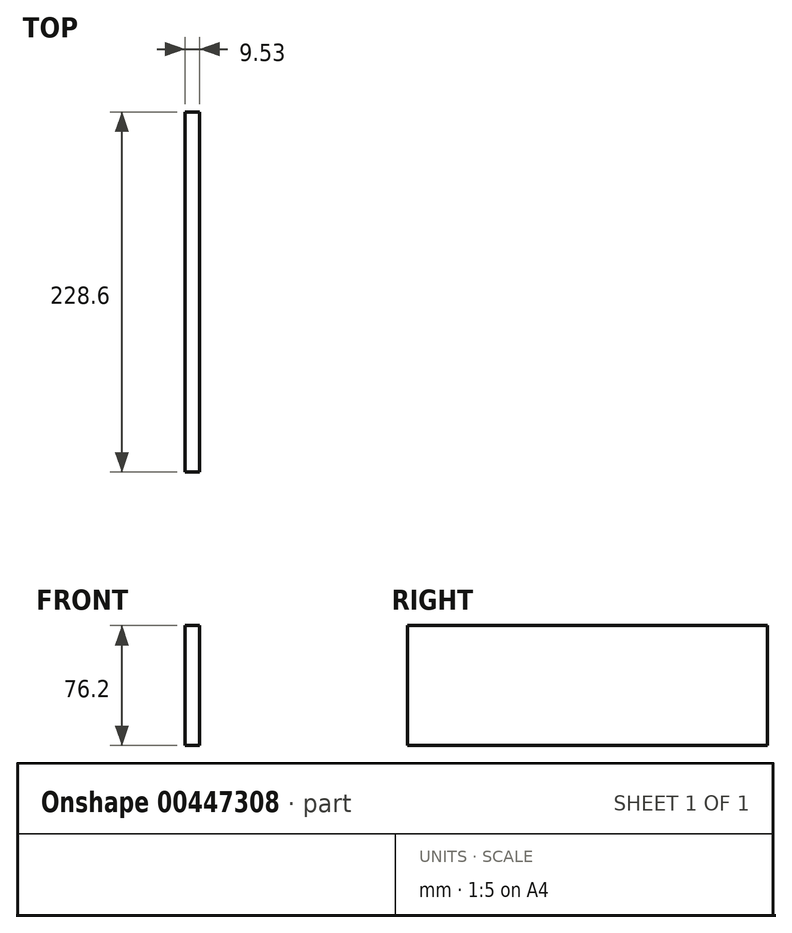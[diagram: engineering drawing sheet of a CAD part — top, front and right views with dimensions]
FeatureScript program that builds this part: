
annotation { "Feature Type Name" : "Feature", "Feature Type Description" : "" }
export const myFeature = defineFeature(function(context is Context, id is Id, definition is map)
    precondition{}
    {
        {
            var Q0;
            Q0=qCreatedBy(makeId("Right.planeOp"),FACE);
            var sketch = newSketch(context, id + "F0", { "sketchPlane" : qUnion([Q0])});
            skLineSegment(sketch, "E0.bottom", {"start": v(-114.3, 38.1) * mm, "end": v(114.3, 38.1) * mm});
            skLineSegment(sketch, "E0.top", {"start": v(-114.3, -38.1) * mm, "end": v(114.3, -38.1) * mm});
            skLineSegment(sketch, "E0.left", {"start": v(-114.3, 38.1) * mm, "end": v(-114.3, -38.1) * mm});
            skLineSegment(sketch, "E0.right", {"start": v(114.3, 38.1) * mm, "end": v(114.3, -38.1) * mm});
            skPoint(sketch, "E0.middle", {"position": v(0, 0) * mm});
            skSolve(sketch);
        }
        {
            var Q0;
            Q0=makeQuery(id+"F0.imprint","IMPRINT",FACE,{"disambiguationData":[TD([[makeQuery(id+"F0.imprint","IMPRINT",EDGE,{"derivedFrom":sQuery(id+"F0.wireOp",EDGE,"E0.bottom")}),-1.0]])]});
            extrude(context, id + "F1", {"entities" : qUnion([Q0]), "depth" : 9.52 * mm});
        }
    });
